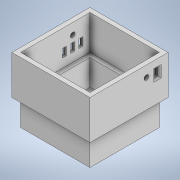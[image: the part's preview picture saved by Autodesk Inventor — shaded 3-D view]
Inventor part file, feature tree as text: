
AUTODESK INVENTOR PART (.ipt)
format: ipt  version: 2020 (Build 240168000, 168)  size: 200,192 bytes
history: native  units: in
note: dims shown in document units (in); Inventor stores cm internally (conversion verified against a paired STEP export)
features: extrude x7, sketch x7, chamfer x2
ambient origin geometry x8: Origin, YZ Plane, XZ Plane, XY Plane, X Axis, Y Axis, Z Axis, Center Point
bodies: Solid1 (feature_tree)
feature tree (16):
  extrude  "Extrusion1"  Depth=3.1496in
  extrude  "Extrusion2"  Depth=0.1969in
  extrude  "Extrusion3"  Depth=0.1969in
  extrude  "Extrusion4"  Depth=1.7717in TaperAngle=0.0deg
  extrude  "Extrusion5"  Depth=0.1969in
  extrude  "Extrusion6"  Depth=0.1969in
  chamfer  "Chamfer1"  Distance=0.1969in
  extrude  "Extrusion7"  Depth=0.1969in
  chamfer  "Chamfer2"  Distance=1.1811in
  sketch  "Sketch1"  dims[d0=3.1496in d1=3.1496in]
  sketch  "Sketch2"  dims[d2=1.1811in d3=0.0in d4=0.1969in]
  sketch  "Sketch3"  dims[d5=0.1969in d6=0.1969in]
  sketch  "Sketch4"  dims[d7=0.1969in d8=1.7717in d9=0.0in]
  sketch  "Sketch5"  dims[d10=0.1969in d11=0.1969in]
  sketch  "Sketch6"  dims[d12=1.5748in d13=0.0in d14=0.1969in]
  sketch  "Sketch8"  dims[d15=0.1969in d16=0.1969in d17=0.1969in d18=1.1811in d19=0.0in d20=0.2165in d21=0.4921in d22=0.9843in d23=0.3937in d24=0.0in d25=0.3937in d26=0.1772in d27=0.374in d28=0.3937in d29=0.3937in d30=0.0in d31=0.0787in d32=0.0787in d33=45.0deg d39=0.1772in d40=0.374in d41=0.1772in d42=0.1772in d43=0.7874in d44=0.9055in d45=0.1969in d46=0.1969in d47=0.3937in d48=0.0in d49=0.0787in d50=0.0787in d51=45.0deg]
